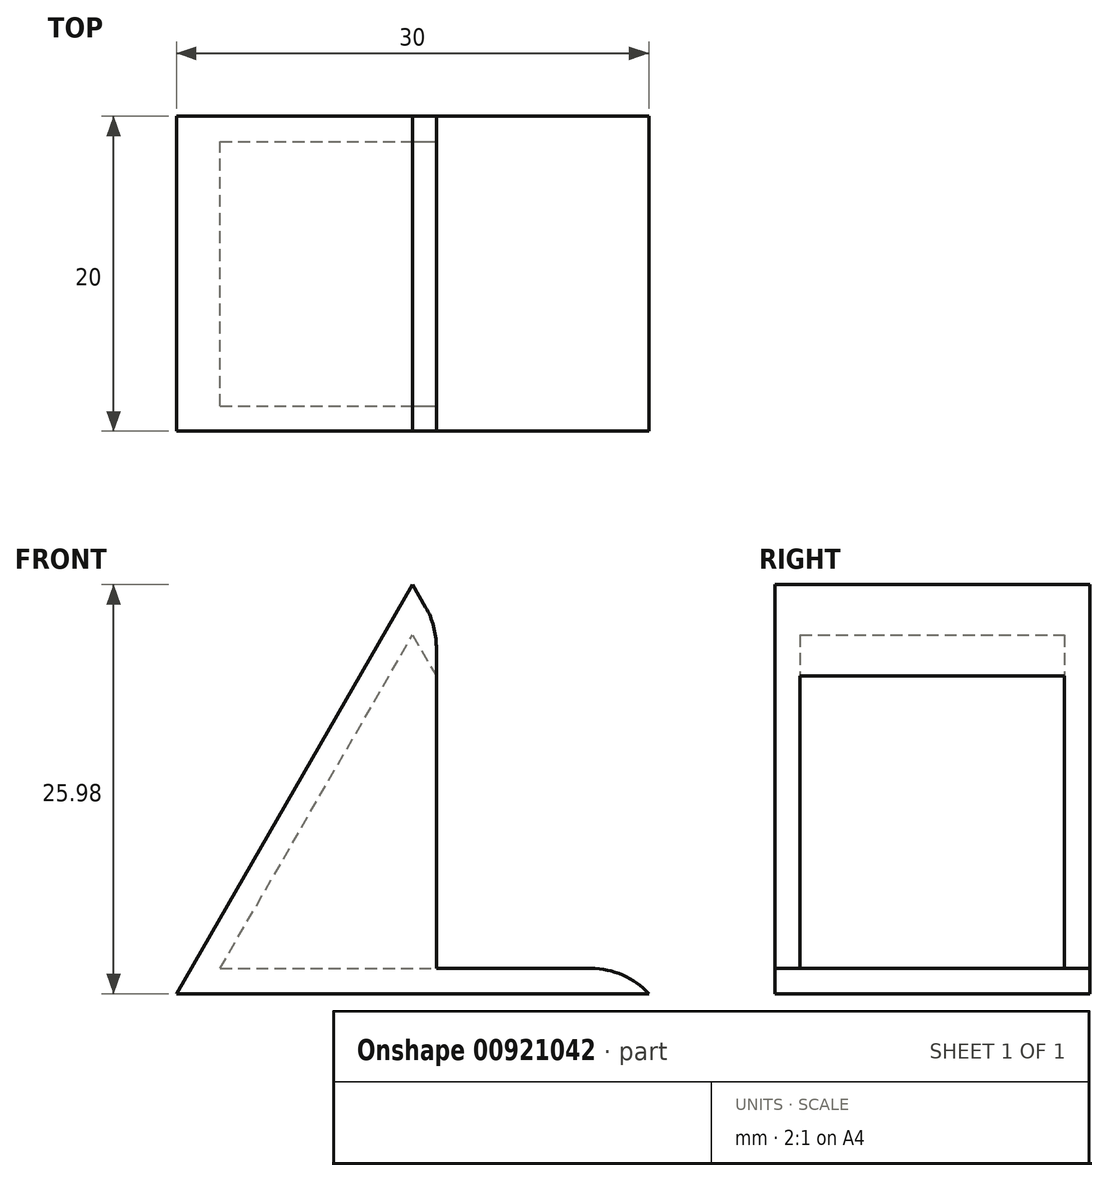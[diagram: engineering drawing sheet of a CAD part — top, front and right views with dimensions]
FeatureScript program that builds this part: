
annotation { "Feature Type Name" : "Feature", "Feature Type Description" : "" }
export const myFeature = defineFeature(function(context is Context, id is Id, definition is map)
    precondition{}
    {
        {
            var Q0;
            Q0=qCreatedBy(makeId("Front.planeOp"),FACE);
            var sketch = newSketch(context, id + "F0", { "sketchPlane" : qUnion([Q0])});
            skLineSegment(sketch, "E0", {"start": v(0, 0) * mm, "end": v(30, 0) * mm});
            skLineSegment(sketch, "E1", {"start": v(0, 0) * mm, "end": v(15, 25.98) * mm});
            skLineSegment(sketch, "E2", {"start": v(15, 25.98) * mm, "end": v(30, 0) * mm});
            skLineSegment(sketch, "E3", {"start": v(15, 25.98) * mm, "end": v(15, 0) * mm, "construction": true});
            skLineSegment(sketch, "E4", {"start": v(16.5, 23.38) * mm, "end": v(16.5, 0) * mm});
            skLineSegment(sketch, "E5", {"start": v(16.5, 1.6) * mm, "end": v(29.08, 1.6) * mm});
            skSolve(sketch);
        }
        {
            var Q0;
            {var subQ4=sQuery(id+"F0.wireOp",EDGE,"E1");Q0=makeQuery(id+"F0.imprint","IMPRINT",FACE,{"disambiguationData":[TD([[makeQuery(id+"F0.imprint","IMPRINT",EDGE,{"derivedFrom":subQ4}),-1.0]])]});}
            var Q1;
            {var subQ5=sQuery(id+"F0.wireOp",EDGE,"E5");Q1=makeQuery(id+"F0.imprint","IMPRINT",FACE,{"disambiguationData":[TD([[makeQuery(id+"F0.imprint","IMPRINT",EDGE,{"derivedFrom":subQ5}),-1.0]])]});}
            extrude(context, id + "F1", {"entities" : qUnion([Q0, Q1]), "depth" : 20 * mm, "offsetDistance" : 25 * mm});
        }
        {
            var Q0;
            Q0=makeQuery(id+"F1.opExtrude","SWEPT_FACE",FACE,{"disambiguationData":[OSD([sQuery(id+"F0.wireOp",EDGE,"E4")])]});
            shell(context, id + "F2", {"entities" : qUnion([Q0]), "thickness" : 1.6 * mm});
        }
        {
            var Q0;
            Q0=makeQuery(id+"F1.opExtrude","SWEPT_EDGE",EDGE,{"disambiguationData":[OSD([sQuery(id+"F0.wireOp",EDGE,"E2"),sQuery(id+"F0.wireOp",EDGE,"E5")])]});
            var Q1;
            Q1=makeQuery(id+"F1.opExtrude","SWEPT_EDGE",EDGE,{"disambiguationData":[OSD([sQuery(id+"F0.wireOp",EDGE,"E2"),sQuery(id+"F0.wireOp",EDGE,"E4")])]});
            fillet(context, id + "F3", {"entities" : qUnion([Q0, Q1]), "radius" : 5 * mm, "tangentPropagation" : true, "allowEdgeOverflow" : false});
        }
    });
